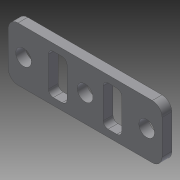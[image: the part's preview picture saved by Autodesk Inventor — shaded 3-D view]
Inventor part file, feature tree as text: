
AUTODESK INVENTOR PART (.ipt)
format: ipt  version: 2015 (Build 190159000, 159)  size: 125,440 bytes
history: native  units: in
note: dims shown in document units (in); Inventor stores cm internally (conversion verified against a paired STEP export)
features: extrude x1, sketch x1
ambient origin geometry x8: Origin, YZ Plane, XZ Plane, XY Plane, X Axis, Y Axis, Z Axis, Center Point
bodies: Solid1 (feature_tree)
feature tree (2):
  extrude  "Extrusion1"  Depth=1.378in
  sketch  "Sketch1"  dims[d0=3.937in d1=1.378in d2=3.1496in d3=0.4016in d4=0.25in d5=0.0in d6=0.4016in d7=0.25in d8=1.0236in d9=0.4764in d10=0.125in d11=1.4in]
